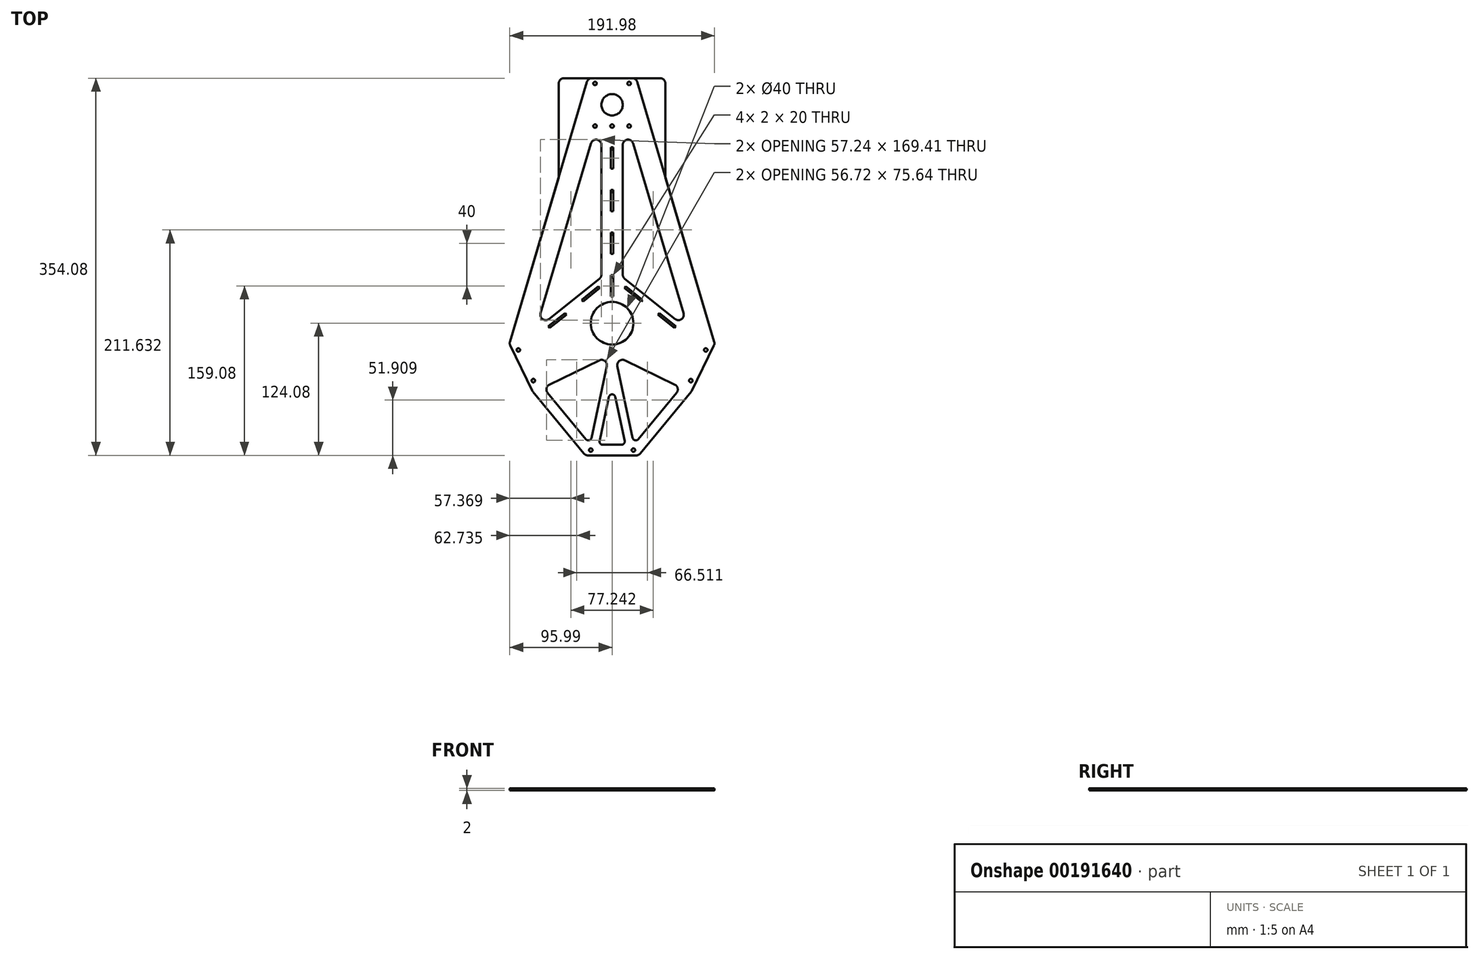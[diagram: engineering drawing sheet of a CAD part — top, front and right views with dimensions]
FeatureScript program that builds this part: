
annotation { "Feature Type Name" : "Feature", "Feature Type Description" : "" }
export const myFeature = defineFeature(function(context is Context, id is Id, definition is map)
    precondition{}
    {
        {
            var Q0;
            Q0=qCreatedBy(makeId("Top.planeOp"),FACE);
            var sketch = newSketch(context, id + "F0", { "sketchPlane" : qUnion([Q0])});
            skLineSegment(sketch, "E0", {"start": v(0, 0) * mm, "end": v(0, 400) * mm, "construction": true});
            skLineSegment(sketch, "E1", {"start": v(-233.64, -114.08) * mm, "end": v(233.64, -114.08) * mm});
            skLineSegment(sketch, "E2", {"start": v(233.64, -114.08) * mm, "end": v(0, 400) * mm});
            skLineSegment(sketch, "E3", {"start": v(0, 400) * mm, "end": v(-233.64, -114.08) * mm});
            skLineSegment(sketch, "E4", {"start": v(0, 0) * mm, "end": v(233.64, -114.08) * mm, "construction": true});
            skLineSegment(sketch, "E5", {"start": v(0, 0) * mm, "end": v(-233.64, -114.08) * mm, "construction": true});
            skCircle(sketch, "E6", {"center": v(233.64, -114.08) * mm, "radius": 150 * mm, "construction": true});
            skCircle(sketch, "E7", {"center": v(-233.64, -114.08) * mm, "radius": 150 * mm, "construction": true});
            skCircle(sketch, "E8", {"center": v(0, 400) * mm, "radius": 150 * mm, "construction": true});
            skSolve(sketch);
        }
        {
            var Q0;
            Q0=qCreatedBy(makeId("Top.planeOp"),FACE);
            var sketch = newSketch(context, id + "F1", { "sketchPlane" : qUnion([Q0])});
            skLineSegment(sketch, "E9", {"start": v(-25, -124.08) * mm, "end": v(25, -124.08) * mm});
            skLineSegment(sketch, "E10", {"start": v(96.34, -19.22) * mm, "end": v(22.5, 230) * mm});
            skLineSegment(sketch, "E11", {"start": v(22.5, 230) * mm, "end": v(-22.5, 230) * mm});
            skLineSegment(sketch, "E12", {"start": v(-22.5, 230) * mm, "end": v(-96.34, -19.22) * mm});
            skLineSegment(sketch, "E13", {"start": v(96.34, -19.22) * mm, "end": v(74.4, -64.15) * mm});
            skLineSegment(sketch, "E14", {"start": v(-96.34, -19.22) * mm, "end": v(-74.4, -64.15) * mm});
            skLineSegment(sketch, "E15", {"start": v(-74.4, -64.15) * mm, "end": v(-25, -124.08) * mm});
            skLineSegment(sketch, "E16", {"start": v(74.4, -64.15) * mm, "end": v(25, -124.08) * mm});
            skLineSegment(sketch, "E17", {"start": v(-19.8, 168.73) * mm, "end": v(-67.04, 9.27) * mm});
            skLineSegment(sketch, "E18", {"start": v(-59.12, 3.94) * mm, "end": v(-11.88, 41.72) * mm});
            skLineSegment(sketch, "E19", {"start": v(-10, 45.62) * mm, "end": v(-10, 167.3) * mm});
            skLineSegment(sketch, "E20.MirrorCS", {"start": v(10, 45.62) * mm, "end": v(10, 167.3) * mm});
            skLineSegment(sketch, "E21.MirrorCS", {"start": v(19.8, 168.73) * mm, "end": v(67.04, 9.27) * mm});
            skLineSegment(sketch, "E22.MirrorCS", {"start": v(59.12, 3.94) * mm, "end": v(11.88, 41.72) * mm});
            skLineSegment(sketch, "E23", {"start": v(-60.47, -65.32) * mm, "end": v(-24.55, -108.9) * mm});
            skLineSegment(sketch, "E24", {"start": v(-19.3, -107.62) * mm, "end": v(-5, -40.37) * mm});
            skLineSegment(sketch, "E25", {"start": v(-12.08, -34.83) * mm, "end": v(-58.8, -57.65) * mm});
            skLineSegment(sketch, "E26.MirrorCS", {"start": v(60.47, -65.32) * mm, "end": v(24.55, -108.9) * mm});
            skLineSegment(sketch, "E27.MirrorCS", {"start": v(19.3, -107.62) * mm, "end": v(5, -40.37) * mm});
            skLineSegment(sketch, "E28.MirrorCS", {"start": v(12.08, -34.83) * mm, "end": v(58.8, -57.65) * mm});
            skLineSegment(sketch, "E29", {"start": v(-2.93, -69.12) * mm, "end": v(-11.73, -110.46) * mm});
            skLineSegment(sketch, "E30", {"start": v(-8.8, -114.08) * mm, "end": v(8.8, -114.08) * mm});
            skLineSegment(sketch, "E31", {"start": v(11.73, -110.46) * mm, "end": v(2.93, -69.12) * mm});
            skCircle(sketch, "E32", {"center": v(0, 0) * mm, "radius": 20 * mm});
            skCircle(sketch, "E33", {"center": v(0, 205) * mm, "radius": 10 * mm});
            skPoint(sketch, "E33.centerSnap0", {"position": v(0, 230) * mm});
            skPoint(sketch, "E34.visualSharp", {"position": v(10, 201.78) * mm});
            skArc(sketch, "E34.filletArc", {"start": v(19.8, 168.73) * mm, "mid": v(14.28, 172.26) * mm, "end": v(10, 167.3) * mm});
            skPoint(sketch, "E35.visualSharp", {"position": v(-10, 201.78) * mm});
            skArc(sketch, "E35.filletArc", {"start": v(-10, 167.3) * mm, "mid": v(-14.28, 172.26) * mm, "end": v(-19.8, 168.73) * mm});
            skLineSegment(sketch, "E36.bottom", {"start": v(1, 165) * mm, "end": v(-1, 165) * mm});
            skLineSegment(sketch, "E36.top", {"start": v(1, 145) * mm, "end": v(-1, 145) * mm});
            skLineSegment(sketch, "E36.left", {"start": v(1, 165) * mm, "end": v(1, 145) * mm});
            skLineSegment(sketch, "E36.right", {"start": v(-1, 165) * mm, "end": v(-1, 145) * mm});
            skLineSegment(sketch, "E37.0.1.0", {"start": v(1, 105) * mm, "end": v(-1, 105) * mm});
            skLineSegment(sketch, "E37.0.1.1", {"start": v(-1, 125) * mm, "end": v(-1, 105) * mm});
            skLineSegment(sketch, "E37.0.1.2", {"start": v(1, 125) * mm, "end": v(1, 105) * mm});
            skLineSegment(sketch, "E37.0.1.3", {"start": v(1, 125) * mm, "end": v(-1, 125) * mm});
            skLineSegment(sketch, "E37.0.2.0", {"start": v(1, 65) * mm, "end": v(-1, 65) * mm});
            skLineSegment(sketch, "E37.0.2.1", {"start": v(-1, 85) * mm, "end": v(-1, 65) * mm});
            skLineSegment(sketch, "E37.0.2.2", {"start": v(1, 85) * mm, "end": v(1, 65) * mm});
            skLineSegment(sketch, "E37.0.2.3", {"start": v(1, 85) * mm, "end": v(-1, 85) * mm});
            skLineSegment(sketch, "E37.0.3.0", {"start": v(1, 25) * mm, "end": v(-1, 25) * mm});
            skLineSegment(sketch, "E37.0.3.1", {"start": v(-1, 45) * mm, "end": v(-1, 25) * mm});
            skLineSegment(sketch, "E37.0.3.2", {"start": v(1, 45) * mm, "end": v(1, 25) * mm});
            skLineSegment(sketch, "E37.0.3.3", {"start": v(1, 45) * mm, "end": v(-1, 45) * mm});
            skLineSegment(sketch, "E37.direction1", {"start": v(-1, 145) * mm, "end": v(6.2, 145) * mm, "construction": true});
            skLineSegment(sketch, "E37.direction2", {"start": v(-1, 145) * mm, "end": v(-1, 105) * mm, "construction": true});
            skLineSegment(sketch, "E38", {"start": v(59.76, -2.97) * mm, "end": v(44.14, 9.52) * mm});
            skLineSegment(sketch, "E39", {"start": v(44.14, 9.52) * mm, "end": v(42.89, 7.96) * mm});
            skLineSegment(sketch, "E40", {"start": v(42.89, 7.96) * mm, "end": v(58.5, -4.53) * mm});
            skLineSegment(sketch, "E41", {"start": v(58.5, -4.53) * mm, "end": v(59.76, -2.97) * mm});
            skLineSegment(sketch, "E42.1.0.0", {"start": v(12.9, 34.5) * mm, "end": v(11.65, 32.94) * mm});
            skLineSegment(sketch, "E42.1.0.1", {"start": v(28.52, 22.01) * mm, "end": v(12.9, 34.5) * mm});
            skLineSegment(sketch, "E42.1.0.2", {"start": v(27.27, 20.45) * mm, "end": v(28.52, 22.01) * mm});
            skLineSegment(sketch, "E42.1.0.3", {"start": v(11.65, 32.94) * mm, "end": v(27.27, 20.45) * mm});
            skLineSegment(sketch, "E42.direction1", {"start": v(42.89, 7.96) * mm, "end": v(11.65, 32.94) * mm, "construction": true});
            skPoint(sketch, "E43.visualSharp", {"position": v(10, 43.22) * mm});
            skArc(sketch, "E43.filletArc", {"start": v(10, 45.62) * mm, "mid": v(10.5, 43.46) * mm, "end": v(11.88, 41.72) * mm});
            skPoint(sketch, "E44.visualSharp", {"position": v(-10, 43.22) * mm});
            skArc(sketch, "E44.filletArc", {"start": v(-11.88, 41.72) * mm, "mid": v(-10.5, 43.46) * mm, "end": v(-10, 45.62) * mm});
            skPoint(sketch, "E45.visualSharp", {"position": v(-71.56, -6) * mm});
            skArc(sketch, "E45.filletArc", {"start": v(-67.04, 9.27) * mm, "mid": v(-65.03, 3.7) * mm, "end": v(-59.12, 3.94) * mm});
            skPoint(sketch, "E46.visualSharp", {"position": v(71.56, -6) * mm});
            skArc(sketch, "E46.filletArc", {"start": v(59.12, 3.94) * mm, "mid": v(65.03, 3.7) * mm, "end": v(67.04, 9.27) * mm});
            skPoint(sketch, "E47.visualSharp", {"position": v(2.86, -30.33) * mm});
            skArc(sketch, "E47.filletArc", {"start": v(12.08, -34.83) * mm, "mid": v(6.8, -35.38) * mm, "end": v(5, -40.37) * mm});
            skPoint(sketch, "E48.visualSharp", {"position": v(-2.86, -30.33) * mm});
            skArc(sketch, "E48.filletArc", {"start": v(-5, -40.37) * mm, "mid": v(-6.8, -35.38) * mm, "end": v(-12.08, -34.83) * mm});
            skPoint(sketch, "E49.visualSharp", {"position": v(-64.5, -60.43) * mm});
            skArc(sketch, "E49.filletArc", {"start": v(-58.8, -57.65) * mm, "mid": v(-61.5, -61.08) * mm, "end": v(-60.47, -65.32) * mm});
            skPoint(sketch, "E50.visualSharp", {"position": v(64.5, -60.43) * mm});
            skArc(sketch, "E50.filletArc", {"start": v(60.47, -65.32) * mm, "mid": v(61.5, -61.08) * mm, "end": v(58.8, -57.65) * mm});
            skPoint(sketch, "E51.visualSharp", {"position": v(20.6, -113.7) * mm});
            skArc(sketch, "E51.filletArc", {"start": v(19.3, -107.62) * mm, "mid": v(21.53, -109.9) * mm, "end": v(24.55, -108.9) * mm});
            skPoint(sketch, "E52.visualSharp", {"position": v(-20.6, -113.7) * mm});
            skArc(sketch, "E52.filletArc", {"start": v(-24.55, -108.9) * mm, "mid": v(-21.53, -109.9) * mm, "end": v(-19.3, -107.62) * mm});
            skPoint(sketch, "E53.visualSharp", {"position": v(-12.5, -114.08) * mm});
            skArc(sketch, "E53.filletArc", {"start": v(-11.73, -110.46) * mm, "mid": v(-11.13, -112.97) * mm, "end": v(-8.8, -114.08) * mm});
            skPoint(sketch, "E54.visualSharp", {"position": v(12.5, -114.08) * mm});
            skArc(sketch, "E54.filletArc", {"start": v(8.8, -114.08) * mm, "mid": v(11.13, -112.97) * mm, "end": v(11.73, -110.46) * mm});
            skPoint(sketch, "E55.visualSharp", {"position": v(0, -55.33) * mm});
            skArc(sketch, "E55.filletArc", {"start": v(2.93, -69.12) * mm, "mid": v(0, -66.75) * mm, "end": v(-2.93, -69.12) * mm});
            skLineSegment(sketch, "E56.MirrorCS", {"start": v(-27.27, 20.45) * mm, "end": v(-28.52, 22.01) * mm});
            skLineSegment(sketch, "E57.MirrorCS", {"start": v(-12.9, 34.5) * mm, "end": v(-11.65, 32.94) * mm});
            skLineSegment(sketch, "E58.MirrorCS", {"start": v(-11.65, 32.94) * mm, "end": v(-27.27, 20.45) * mm});
            skLineSegment(sketch, "E59.MirrorCS", {"start": v(-28.52, 22.01) * mm, "end": v(-12.9, 34.5) * mm});
            skLineSegment(sketch, "E60.MirrorCS", {"start": v(-44.14, 9.52) * mm, "end": v(-42.89, 7.96) * mm});
            skLineSegment(sketch, "E61.MirrorCS", {"start": v(-58.5, -4.53) * mm, "end": v(-59.76, -2.97) * mm});
            skLineSegment(sketch, "E62.MirrorCS", {"start": v(-59.76, -2.97) * mm, "end": v(-44.14, 9.52) * mm});
            skLineSegment(sketch, "E63.MirrorCS", {"start": v(-42.89, 7.96) * mm, "end": v(-58.5, -4.53) * mm});
            skSolve(sketch);
        }
        {
            var Q0;
            Q0=makeQuery(id+"F1.imprint","IMPRINT",FACE,{"disambiguationData":[TD([[makeQuery(id+"F1.imprint","IMPRINT",EDGE,{"derivedFrom":sQuery(id+"F1.wireOp",EDGE,"E9")}),1.0]])]});
            extrude(context, id + "F2", {"entities" : qUnion([Q0]), "depth" : 2 * mm});
        }
        {
            var Q0;
            Q0=makeQuery(id+"F2.opExtrude","SWEPT_EDGE",EDGE,{"disambiguationData":[OSD([sQuery(id+"F1.wireOp",EDGE,"E9"),sQuery(id+"F1.wireOp",EDGE,"E15")])]});
            var Q1;
            Q1=makeQuery(id+"F2.opExtrude","SWEPT_EDGE",EDGE,{"disambiguationData":[OSD([sQuery(id+"F1.wireOp",EDGE,"E9"),sQuery(id+"F1.wireOp",EDGE,"E16")])]});
            var Q2;
            Q2=makeQuery(id+"F2.opExtrude","SWEPT_EDGE",EDGE,{"disambiguationData":[OSD([sQuery(id+"F1.wireOp",EDGE,"E14"),sQuery(id+"F1.wireOp",EDGE,"E15")])]});
            var Q3;
            Q3=makeQuery(id+"F2.opExtrude","SWEPT_EDGE",EDGE,{"disambiguationData":[OSD([sQuery(id+"F1.wireOp",EDGE,"E12"),sQuery(id+"F1.wireOp",EDGE,"E14")])]});
            var Q4;
            Q4=makeQuery(id+"F2.opExtrude","SWEPT_EDGE",EDGE,{"disambiguationData":[OSD([sQuery(id+"F1.wireOp",EDGE,"E13"),sQuery(id+"F1.wireOp",EDGE,"E16")])]});
            var Q5;
            Q5=makeQuery(id+"F2.opExtrude","SWEPT_EDGE",EDGE,{"disambiguationData":[OSD([sQuery(id+"F1.wireOp",EDGE,"E10"),sQuery(id+"F1.wireOp",EDGE,"E13")])]});
            var Q6;
            Q6=makeQuery(id+"F2.opExtrude","SWEPT_EDGE",EDGE,{"disambiguationData":[OSD([sQuery(id+"F1.wireOp",EDGE,"E10"),sQuery(id+"F1.wireOp",EDGE,"E11")])]});
            var Q7;
            Q7=makeQuery(id+"F2.opExtrude","SWEPT_EDGE",EDGE,{"disambiguationData":[OSD([sQuery(id+"F1.wireOp",EDGE,"E11"),sQuery(id+"F1.wireOp",EDGE,"E12")])]});
            fillet(context, id + "F3", {"entities" : qUnion([Q0, Q1, Q2, Q3, Q4, Q5, Q6, Q7]), "radius" : 5 * mm, "tangentPropagation" : true, "allowEdgeOverflow" : false});
        }
        {
            var Q0;
            Q0=makeQuery(id+"F2.opExtrude","CAP_FACE",FACE,{"disambiguationData":[OSD([sQuery(id+"F1.wireOp",EDGE,"E9"),sQuery(id+"F1.wireOp",EDGE,"E10"),sQuery(id+"F1.wireOp",EDGE,"E11"),sQuery(id+"F1.wireOp",EDGE,"E12"),sQuery(id+"F1.wireOp",EDGE,"E13"),sQuery(id+"F1.wireOp",EDGE,"E14"),sQuery(id+"F1.wireOp",EDGE,"E15"),sQuery(id+"F1.wireOp",EDGE,"E16"),sQuery(id+"F1.wireOp",EDGE,"E17"),sQuery(id+"F1.wireOp",EDGE,"E18"),sQuery(id+"F1.wireOp",EDGE,"E19"),sQuery(id+"F1.wireOp",EDGE,"E20.MirrorCS"),sQuery(id+"F1.wireOp",EDGE,"E21.MirrorCS"),sQuery(id+"F1.wireOp",EDGE,"E22.MirrorCS"),sQuery(id+"F1.wireOp",EDGE,"E23"),sQuery(id+"F1.wireOp",EDGE,"E24"),sQuery(id+"F1.wireOp",EDGE,"E25"),sQuery(id+"F1.wireOp",EDGE,"E26.MirrorCS"),sQuery(id+"F1.wireOp",EDGE,"E27.MirrorCS"),sQuery(id+"F1.wireOp",EDGE,"E28.MirrorCS"),sQuery(id+"F1.wireOp",EDGE,"E29"),sQuery(id+"F1.wireOp",EDGE,"E30"),sQuery(id+"F1.wireOp",EDGE,"E31"),sQuery(id+"F1.wireOp",EDGE,"E32")])],"isStart":false});
            var sketch = newSketch(context, id + "F4", { "sketchPlane" : qUnion([Q0])});
            skPoint(sketch, "E64", {"position": v(-16, 225) * mm});
            skPoint(sketch, "E65", {"position": v(16, 225) * mm});
            skPoint(sketch, "E66", {"position": v(-16, 185) * mm});
            skPoint(sketch, "E67", {"position": v(16, 185) * mm});
            skPoint(sketch, "E68", {"position": v(0, 185) * mm});
            skPoint(sketch, "E69", {"position": v(-20, -119.08) * mm});
            skPoint(sketch, "E70", {"position": v(20, -119.08) * mm});
            skPoint(sketch, "E71", {"position": v(87.9, -25.11) * mm});
            skPoint(sketch, "E72", {"position": v(73.85, -53.87) * mm});
            skPoint(sketch, "E73", {"position": v(-87.9, -25.11) * mm});
            skPoint(sketch, "E74", {"position": v(-73.85, -53.87) * mm});
            skSolve(sketch);
        }
        {
            var Q0;
            Q0=sQuery(id+"F4.wireOp",VERTEX,"E66");
            var Q1;
            Q1=sQuery(id+"F4.wireOp",VERTEX,"E67");
            var Q2;
            Q2=sQuery(id+"F4.wireOp",VERTEX,"E68");
            var Q3;
            Q3=sQuery(id+"F4.wireOp",VERTEX,"E65");
            var Q4;
            Q4=sQuery(id+"F4.wireOp",VERTEX,"E64");
            var Q5;
            Q5=sQuery(id+"F4.wireOp",VERTEX,"E73");
            var Q6;
            Q6=sQuery(id+"F4.wireOp",VERTEX,"E74");
            var Q7;
            Q7=sQuery(id+"F4.wireOp",VERTEX,"E69");
            var Q8;
            Q8=sQuery(id+"F4.wireOp",VERTEX,"E70");
            var Q9;
            Q9=sQuery(id+"F4.wireOp",VERTEX,"E72");
            var Q10;
            Q10=sQuery(id+"F4.wireOp",VERTEX,"E71");
            var Q11;
            Q11=makeQuery(id+"F2.opExtrude","SWEPT_BODY",BODY,{"disambiguationData":[OSD([sQuery(id+"F1.wireOp",EDGE,"E9"),sQuery(id+"F1.wireOp",EDGE,"E10"),sQuery(id+"F1.wireOp",EDGE,"E11"),sQuery(id+"F1.wireOp",EDGE,"E12"),sQuery(id+"F1.wireOp",EDGE,"E13"),sQuery(id+"F1.wireOp",EDGE,"E14"),sQuery(id+"F1.wireOp",EDGE,"E15"),sQuery(id+"F1.wireOp",EDGE,"E16"),sQuery(id+"F1.wireOp",EDGE,"E17"),sQuery(id+"F1.wireOp",EDGE,"E18"),sQuery(id+"F1.wireOp",EDGE,"E19"),sQuery(id+"F1.wireOp",EDGE,"E20.MirrorCS"),sQuery(id+"F1.wireOp",EDGE,"E21.MirrorCS"),sQuery(id+"F1.wireOp",EDGE,"E22.MirrorCS"),sQuery(id+"F1.wireOp",EDGE,"E23"),sQuery(id+"F1.wireOp",EDGE,"E24"),sQuery(id+"F1.wireOp",EDGE,"E25"),sQuery(id+"F1.wireOp",EDGE,"E26.MirrorCS"),sQuery(id+"F1.wireOp",EDGE,"E27.MirrorCS"),sQuery(id+"F1.wireOp",EDGE,"E28.MirrorCS"),sQuery(id+"F1.wireOp",EDGE,"E29"),sQuery(id+"F1.wireOp",EDGE,"E30"),sQuery(id+"F1.wireOp",EDGE,"E31"),sQuery(id+"F1.wireOp",EDGE,"E32")])]});
            hole(context, id + "F5", {"style" : HoleStyle.SIMPLE, "endStyle" : HoleEndStyle.THROUGH, "standardTappedOrClearance" : lookupTablePath({ "standard" : "ISO", "fit" : "Normal", "size" : "M3", "type" : "Clearance" }), "standardBlindInLast" : lookupTablePath({ "fit" : "Standard", "standard" : "ISO", "size" : "M3", "type" : "Clearance" }), "holeDiameter" : 3.3 * mm, "isTappedThrough" : true, "tappedDepth" : 6.2 * mm, "tapClearance" : 3, "locations" : qUnion([Q0, Q1, Q2, Q3, Q4, Q5, Q6, Q7, Q8, Q9, Q10]), "scope" : qUnion([Q11])});
        }
        {
            var Q0;
            Q0=qCreatedBy(makeId("Top.planeOp"),FACE);
            var sketch = newSketch(context, id + "F6", { "sketchPlane" : qUnion([Q0])});
            skLineSegment(sketch, "E75.0", {"start": v(-74.4, -64.15) * mm, "end": v(-25, -124.08) * mm});
            skLineSegment(sketch, "E76.0", {"start": v(-25, -124.08) * mm, "end": v(25, -124.08) * mm});
            skLineSegment(sketch, "E77.0", {"start": v(74.4, -64.15) * mm, "end": v(25, -124.08) * mm});
            skLineSegment(sketch, "E78.0", {"start": v(96.34, -19.22) * mm, "end": v(74.4, -64.15) * mm});
            skLineSegment(sketch, "E79.0", {"start": v(12.08, -34.83) * mm, "end": v(58.8, -57.65) * mm});
            skLineSegment(sketch, "E80.0", {"start": v(19.3, -107.62) * mm, "end": v(5, -40.37) * mm});
            skLineSegment(sketch, "E81.0", {"start": v(60.47, -65.32) * mm, "end": v(24.55, -108.9) * mm});
            skLineSegment(sketch, "E82.0", {"start": v(11.73, -110.46) * mm, "end": v(2.93, -69.12) * mm});
            skLineSegment(sketch, "E83.0", {"start": v(-2.93, -69.12) * mm, "end": v(-11.73, -110.46) * mm});
            skLineSegment(sketch, "E84.0", {"start": v(-8.8, -114.08) * mm, "end": v(8.8, -114.08) * mm});
            skLineSegment(sketch, "E85.0", {"start": v(-19.3, -107.62) * mm, "end": v(-5, -40.37) * mm});
            skLineSegment(sketch, "E85.1", {"start": v(-60.47, -65.32) * mm, "end": v(-24.55, -108.9) * mm});
            skLineSegment(sketch, "E85.2", {"start": v(-12.08, -34.83) * mm, "end": v(-58.8, -57.65) * mm});
            skLineSegment(sketch, "E85.3", {"start": v(-96.34, -19.22) * mm, "end": v(-74.4, -64.15) * mm});
            skCircle(sketch, "E86.0", {"center": v(0, 0) * mm, "radius": 20 * mm});
            skLineSegment(sketch, "E87.0", {"start": v(10, 45.62) * mm, "end": v(10, 167.3) * mm});
            skLineSegment(sketch, "E87.1", {"start": v(59.12, 3.94) * mm, "end": v(11.88, 41.72) * mm});
            skLineSegment(sketch, "E87.2", {"start": v(-59.12, 3.94) * mm, "end": v(-11.88, 41.72) * mm});
            skLineSegment(sketch, "E87.3", {"start": v(-10, 45.62) * mm, "end": v(-10, 167.3) * mm});
            skLineSegment(sketch, "E88", {"start": v(-96.34, -19.22) * mm, "end": v(-50, 136.37) * mm});
            skLineSegment(sketch, "E89", {"start": v(-50, 136.37) * mm, "end": v(-50, 230) * mm});
            skLineSegment(sketch, "E90", {"start": v(-50, 230) * mm, "end": v(50, 230) * mm});
            skLineSegment(sketch, "E91", {"start": v(50, 230) * mm, "end": v(50, 136.37) * mm});
            skLineSegment(sketch, "E92", {"start": v(50, 136.37) * mm, "end": v(96.34, -19.22) * mm});
            skLineSegment(sketch, "E93.0", {"start": v(-19.8, 168.73) * mm, "end": v(-67.04, 9.27) * mm});
            skLineSegment(sketch, "E94.0", {"start": v(19.8, 168.73) * mm, "end": v(67.04, 9.27) * mm});
            skSolve(sketch);
        }
        {
            var Q0;
            Q0=makeQuery(id+"F6.imprint","IMPRINT",FACE,{"disambiguationData":[TD([[makeQuery(id+"F6.imprint","IMPRINT",EDGE,{"derivedFrom":sQuery(id+"F6.wireOp",EDGE,"E75.0")}),1.0]])]});
            extrude(context, id + "F7", {"entities" : qUnion([Q0]), "depth" : 2 * mm});
        }
        {
            var Q0;
            Q0=makeQuery(id+"F7.opExtrude","SWEPT_EDGE",EDGE,{"disambiguationData":[OSD([sQuery(id+"F6.wireOp",EDGE,"E85.0"),sQuery(id+"F6.wireOp",EDGE,"E85.2")])]});
            var Q1;
            Q1=makeQuery(id+"F7.opExtrude","SWEPT_EDGE",EDGE,{"disambiguationData":[OSD([sQuery(id+"F6.wireOp",EDGE,"E85.1"),sQuery(id+"F6.wireOp",EDGE,"E85.2")])]});
            var Q2;
            Q2=makeQuery(id+"F7.opExtrude","SWEPT_EDGE",EDGE,{"disambiguationData":[OSD([sQuery(id+"F6.wireOp",EDGE,"E85.0"),sQuery(id+"F6.wireOp",EDGE,"E85.1")])]});
            var Q3;
            Q3=makeQuery(id+"F7.opExtrude","SWEPT_EDGE",EDGE,{"disambiguationData":[OSD([sQuery(id+"F6.wireOp",EDGE,"E82.0"),sQuery(id+"F6.wireOp",EDGE,"E84.0")])]});
            var Q4;
            Q4=makeQuery(id+"F7.opExtrude","SWEPT_EDGE",EDGE,{"disambiguationData":[OSD([sQuery(id+"F6.wireOp",EDGE,"E83.0"),sQuery(id+"F6.wireOp",EDGE,"E84.0")])]});
            var Q5;
            Q5=makeQuery(id+"F7.opExtrude","SWEPT_EDGE",EDGE,{"disambiguationData":[OSD([sQuery(id+"F6.wireOp",EDGE,"E82.0"),sQuery(id+"F6.wireOp",EDGE,"E83.0")])]});
            var Q6;
            Q6=makeQuery(id+"F7.opExtrude","SWEPT_EDGE",EDGE,{"disambiguationData":[OSD([sQuery(id+"F6.wireOp",EDGE,"E79.0"),sQuery(id+"F6.wireOp",EDGE,"E80.0")])]});
            var Q7;
            Q7=makeQuery(id+"F7.opExtrude","SWEPT_EDGE",EDGE,{"disambiguationData":[OSD([sQuery(id+"F6.wireOp",EDGE,"E79.0"),sQuery(id+"F6.wireOp",EDGE,"E81.0")])]});
            var Q8;
            Q8=makeQuery(id+"F7.opExtrude","SWEPT_EDGE",EDGE,{"disambiguationData":[OSD([sQuery(id+"F6.wireOp",EDGE,"E80.0"),sQuery(id+"F6.wireOp",EDGE,"E81.0")])]});
            var Q9;
            Q9=makeQuery(id+"F7.opExtrude","SWEPT_EDGE",EDGE,{"disambiguationData":[OSD([sQuery(id+"F6.wireOp",EDGE,"E87.2"),sQuery(id+"F6.wireOp",EDGE,"E87.3")])]});
            var Q10;
            Q10=makeQuery(id+"F7.opExtrude","SWEPT_EDGE",EDGE,{"disambiguationData":[OSD([sQuery(id+"F6.wireOp",EDGE,"E87.1"),sQuery(id+"F6.wireOp",EDGE,"E94.0")])]});
            var Q11;
            Q11=makeQuery(id+"F7.opExtrude","SWEPT_EDGE",EDGE,{"disambiguationData":[OSD([sQuery(id+"F6.wireOp",EDGE,"E87.0"),sQuery(id+"F6.wireOp",EDGE,"E87.1")])]});
            var Q12;
            Q12=makeQuery(id+"F7.opExtrude","SWEPT_EDGE",EDGE,{"disambiguationData":[OSD([sQuery(id+"F6.wireOp",EDGE,"E87.0"),sQuery(id+"F6.wireOp",EDGE,"E94.0")])]});
            var Q13;
            Q13=makeQuery(id+"F7.opExtrude","SWEPT_EDGE",EDGE,{"disambiguationData":[OSD([sQuery(id+"F6.wireOp",EDGE,"E87.3"),sQuery(id+"F6.wireOp",EDGE,"E93.0")])]});
            var Q14;
            Q14=makeQuery(id+"F7.opExtrude","SWEPT_EDGE",EDGE,{"disambiguationData":[OSD([sQuery(id+"F6.wireOp",EDGE,"E87.2"),sQuery(id+"F6.wireOp",EDGE,"E93.0")])]});
            var Q15;
            Q15=makeQuery(id+"F7.opExtrude","SWEPT_EDGE",EDGE,{"disambiguationData":[OSD([sQuery(id+"F6.wireOp",EDGE,"E76.0"),sQuery(id+"F6.wireOp",EDGE,"E77.0")])]});
            var Q16;
            Q16=makeQuery(id+"F7.opExtrude","SWEPT_EDGE",EDGE,{"disambiguationData":[OSD([sQuery(id+"F6.wireOp",EDGE,"E75.0"),sQuery(id+"F6.wireOp",EDGE,"E76.0")])]});
            var Q17;
            Q17=makeQuery(id+"F7.opExtrude","SWEPT_EDGE",EDGE,{"disambiguationData":[OSD([sQuery(id+"F6.wireOp",EDGE,"E77.0"),sQuery(id+"F6.wireOp",EDGE,"E78.0")])]});
            var Q18;
            Q18=makeQuery(id+"F7.opExtrude","SWEPT_EDGE",EDGE,{"disambiguationData":[OSD([sQuery(id+"F6.wireOp",EDGE,"E78.0"),sQuery(id+"F6.wireOp",EDGE,"E92")])]});
            var Q19;
            Q19=makeQuery(id+"F7.opExtrude","SWEPT_EDGE",EDGE,{"disambiguationData":[OSD([sQuery(id+"F6.wireOp",EDGE,"E75.0"),sQuery(id+"F6.wireOp",EDGE,"E85.3")])]});
            var Q20;
            Q20=makeQuery(id+"F7.opExtrude","SWEPT_EDGE",EDGE,{"disambiguationData":[OSD([sQuery(id+"F6.wireOp",EDGE,"E85.3"),sQuery(id+"F6.wireOp",EDGE,"E88")])]});
            var Q21;
            Q21=makeQuery(id+"F7.opExtrude","SWEPT_EDGE",EDGE,{"disambiguationData":[OSD([sQuery(id+"F6.wireOp",EDGE,"E88"),sQuery(id+"F6.wireOp",EDGE,"E89")])]});
            var Q22;
            Q22=makeQuery(id+"F7.opExtrude","SWEPT_EDGE",EDGE,{"disambiguationData":[OSD([sQuery(id+"F6.wireOp",EDGE,"E91"),sQuery(id+"F6.wireOp",EDGE,"E92")])]});
            var Q23;
            Q23=makeQuery(id+"F7.opExtrude","SWEPT_EDGE",EDGE,{"disambiguationData":[OSD([sQuery(id+"F6.wireOp",EDGE,"E90"),sQuery(id+"F6.wireOp",EDGE,"E91")])]});
            var Q24;
            Q24=makeQuery(id+"F7.opExtrude","SWEPT_EDGE",EDGE,{"disambiguationData":[OSD([sQuery(id+"F6.wireOp",EDGE,"E89"),sQuery(id+"F6.wireOp",EDGE,"E90")])]});
            fillet(context, id + "F8", {"entities" : qUnion([Q0, Q1, Q2, Q3, Q4, Q5, Q6, Q7, Q8, Q9, Q10, Q11, Q12, Q13, Q14, Q15, Q16, Q17, Q18, Q19, Q20, Q21, Q22, Q23, Q24]), "radius" : 5 * mm, "tangentPropagation" : true, "allowEdgeOverflow" : false});
        }
    });
